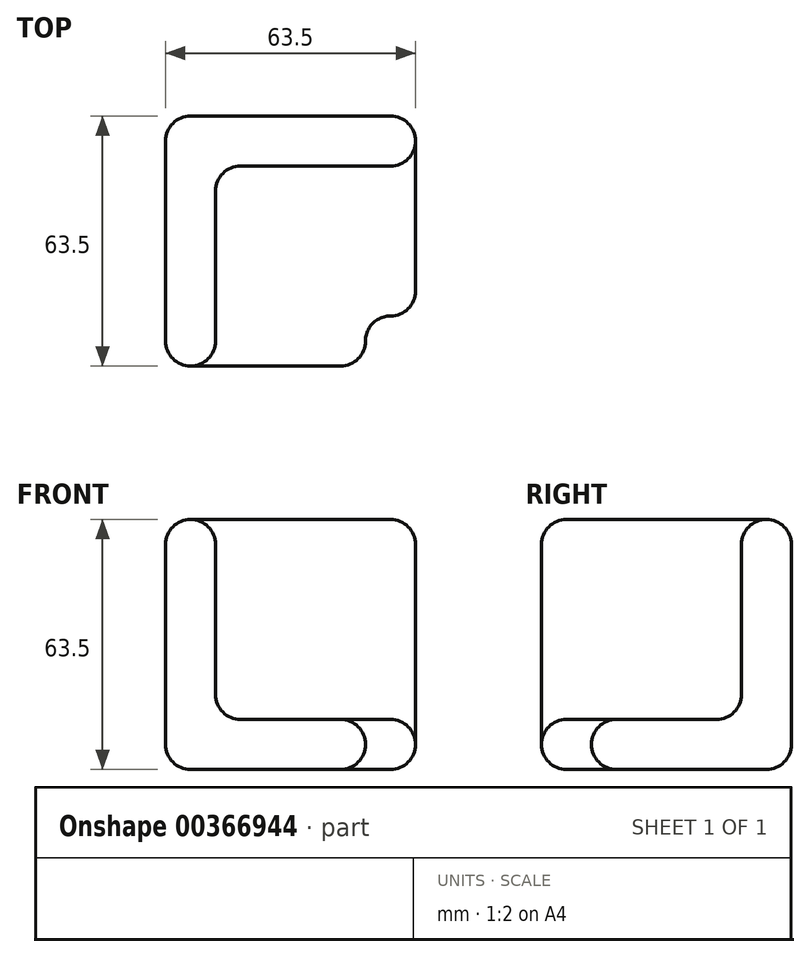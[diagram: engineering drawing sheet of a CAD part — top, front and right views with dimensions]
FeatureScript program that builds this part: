
annotation { "Feature Type Name" : "Feature", "Feature Type Description" : "" }
export const myFeature = defineFeature(function(context is Context, id is Id, definition is map)
    precondition{}
    {
        {
            var Q0;
            Q0=qCreatedBy(makeId("Front.planeOp"),FACE);
            var sketch = newSketch(context, id + "F0", { "sketchPlane" : qUnion([Q0])});
            skLineSegment(sketch, "E0.bottom", {"start": v(0, 0) * mm, "end": v(63.5, 0) * mm});
            skLineSegment(sketch, "E0.top", {"start": v(0, -63.5) * mm, "end": v(63.5, -63.5) * mm});
            skLineSegment(sketch, "E0.left", {"start": v(0, 0) * mm, "end": v(0, -63.5) * mm});
            skLineSegment(sketch, "E0.right", {"start": v(63.5, 0) * mm, "end": v(63.5, -63.5) * mm});
            skSolve(sketch);
        }
        {
            var Q0;
            Q0=makeQuery(id+"F0.imprint","IMPRINT",FACE,{"disambiguationData":[TD([[makeQuery(id+"F0.imprint","IMPRINT",EDGE,{"derivedFrom":sQuery(id+"F0.wireOp",EDGE,"E0.bottom")}),-1.0]])]});
            extrude(context, id + "F1", {"entities" : qUnion([Q0]), "depth" : 63.5 * mm});
        }
        {
            var Q0;
            Q0=makeQuery(id+"F1.opExtrude","SWEPT_FACE",FACE,{"disambiguationData":[OSD([sQuery(id+"F0.wireOp",EDGE,"E0.bottom")])]});
            var sketch = newSketch(context, id + "F2", { "sketchPlane" : qUnion([Q0])});
            skLineSegment(sketch, "E1.bottom", {"start": v(63.5, -63.5) * mm, "end": v(12.7, -63.5) * mm});
            skLineSegment(sketch, "E1.top", {"start": v(63.5, -12.7) * mm, "end": v(12.7, -12.7) * mm});
            skLineSegment(sketch, "E1.left", {"start": v(63.5, -63.5) * mm, "end": v(63.5, -12.7) * mm});
            skLineSegment(sketch, "E1.right", {"start": v(12.7, -63.5) * mm, "end": v(12.7, -12.7) * mm});
            skSolve(sketch);
        }
        {
            var Q0;
            Q0=makeQuery(id+"F2.imprint","IMPRINT",FACE,{"disambiguationData":[TD([[makeQuery(id+"F2.imprint","IMPRINT",EDGE,{"derivedFrom":sQuery(id+"F2.wireOp",EDGE,"E1.bottom")}),1.0]])]});
            extrude(context, id + "F3", {"entities" : qUnion([Q0]), "operationType" : NewBodyOperationType.REMOVE, "oppositeDirection" : true, "depth" : 50.8 * mm});
        }
        {
            var Q0;
            Q0=makeQuery(id+"F3.boolean.opBoolean","COPY",FACE,{"derivedFrom":makeQuery(id+"F3.opExtrude","CAP_FACE",FACE,{"disambiguationData":[OSD([sQuery(id+"F2.wireOp",EDGE,"E1.bottom"),sQuery(id+"F2.wireOp",EDGE,"E1.top"),sQuery(id+"F2.wireOp",EDGE,"E1.left"),sQuery(id+"F2.wireOp",EDGE,"E1.right")])],"isStart":false})});
            var sketch = newSketch(context, id + "F4", { "sketchPlane" : qUnion([Q0])});
            skLineSegment(sketch, "E2.bottom", {"start": v(63.5, -63.5) * mm, "end": v(50.8, -63.5) * mm});
            skLineSegment(sketch, "E2.top", {"start": v(63.5, -50.8) * mm, "end": v(50.8, -50.8) * mm});
            skLineSegment(sketch, "E2.left", {"start": v(63.5, -63.5) * mm, "end": v(63.5, -50.8) * mm});
            skLineSegment(sketch, "E2.right", {"start": v(50.8, -63.5) * mm, "end": v(50.8, -50.8) * mm});
            skSolve(sketch);
        }
        {
            var Q0;
            Q0=makeQuery(id+"F4.imprint","IMPRINT",FACE,{"disambiguationData":[TD([[makeQuery(id+"F4.imprint","IMPRINT",EDGE,{"derivedFrom":sQuery(id+"F4.wireOp",EDGE,"E2.bottom")}),1.0]])]});
            extrude(context, id + "F5", {"entities" : qUnion([Q0]), "operationType" : NewBodyOperationType.REMOVE, "oppositeDirection" : true, "depth" : 12.7 * mm});
        }
        {
            var Q0;
            Q0=makeQuery(id+"F1.opExtrude","SWEPT_FACE",FACE,{"disambiguationData":[OSD([sQuery(id+"F0.wireOp",EDGE,"E0.bottom")])]});
            var Q1;
            Q1=makeQuery(id+"F5.boolean.opBoolean","COPY",FACE,{"derivedFrom":makeQuery(id+"F5.opExtrude","SWEPT_FACE",FACE,{"disambiguationData":[OSD([sQuery(id+"F4.wireOp",EDGE,"E2.top")])]})});
            var Q2;
            Q2=makeQuery(id+"F3.boolean.opBoolean","COPY",FACE,{"derivedFrom":makeQuery(id+"F3.opExtrude","CAP_FACE",FACE,{"disambiguationData":[OSD([sQuery(id+"F2.wireOp",EDGE,"E1.bottom"),sQuery(id+"F2.wireOp",EDGE,"E1.top"),sQuery(id+"F2.wireOp",EDGE,"E1.left"),sQuery(id+"F2.wireOp",EDGE,"E1.right")])],"isStart":false})});
            var Q3;
            Q3=makeQuery(id+"F1.opExtrude","SWEPT_FACE",FACE,{"disambiguationData":[OSD([sQuery(id+"F0.wireOp",EDGE,"E0.right")])]});
            var Q4;
            Q4=makeQuery(id+"F1.opExtrude","CAP_FACE",FACE,{"disambiguationData":[OSD([sQuery(id+"F0.wireOp",EDGE,"E0.bottom"),sQuery(id+"F0.wireOp",EDGE,"E0.top"),sQuery(id+"F0.wireOp",EDGE,"E0.left"),sQuery(id+"F0.wireOp",EDGE,"E0.right")])],"isStart":false});
            var Q5;
            Q5=makeQuery(id+"F5.boolean.opBoolean","COPY",FACE,{"derivedFrom":makeQuery(id+"F5.opExtrude","SWEPT_FACE",FACE,{"disambiguationData":[OSD([sQuery(id+"F4.wireOp",EDGE,"E2.right")])]})});
            var Q6;
            Q6=makeQuery(id+"F1.opExtrude","SWEPT_FACE",FACE,{"disambiguationData":[OSD([sQuery(id+"F0.wireOp",EDGE,"E0.top")])]});
            var Q7;
            Q7=makeQuery(id+"F3.boolean.opBoolean","COPY",FACE,{"derivedFrom":makeQuery(id+"F3.opExtrude","SWEPT_FACE",FACE,{"disambiguationData":[OSD([sQuery(id+"F2.wireOp",EDGE,"E1.top")])]})});
            var Q8;
            Q8=makeQuery(id+"F3.boolean.opBoolean","COPY",FACE,{"derivedFrom":makeQuery(id+"F3.opExtrude","SWEPT_FACE",FACE,{"disambiguationData":[OSD([sQuery(id+"F2.wireOp",EDGE,"E1.right")])]})});
            var Q9;
            Q9=makeQuery(id+"F1.opExtrude","SWEPT_FACE",FACE,{"disambiguationData":[OSD([sQuery(id+"F0.wireOp",EDGE,"E0.left")])]});
            fillet(context, id + "F6", {"entities" : qUnion([Q0, Q1, Q2, Q3, Q4, Q5, Q6, Q7, Q8, Q9]), "radius" : 6.35 * mm, "tangentPropagation" : true, "allowEdgeOverflow" : false});
        }
    });
